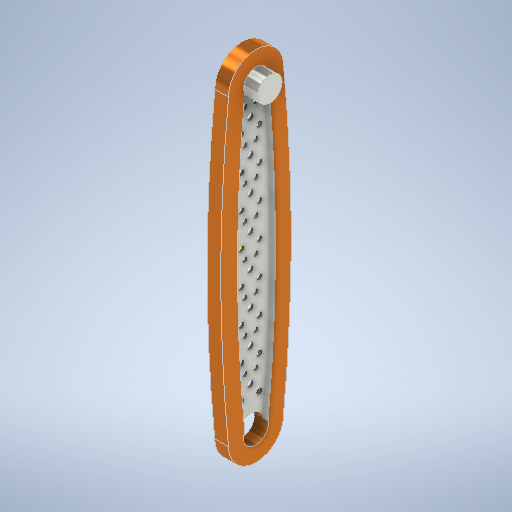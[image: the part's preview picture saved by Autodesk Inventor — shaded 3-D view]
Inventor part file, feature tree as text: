
AUTODESK INVENTOR PART (.ipt)
format: ipt  version: 2025 (Build 290162000, 162)  size: 450,560 bytes
history: native  units: in
note: dims shown in document units (in); Inventor stores cm internally (conversion verified against a paired STEP export)
features: sketch x6, extrude x5, pattern_linear x1
ambient origin geometry x8: Origin, YZ Plane, XZ Plane, XY Plane, X Axis, Y Axis, Z Axis, Center Point
bodies: Solid1 (feature_tree)
feature tree (12):
  extrude  "Extrusion1"  Depth=0.3543in
  sketch  "Sketch2"  dims[d5=0.3543in d6=4.3307in]
  extrude  "Extrusion2"  Depth=4.3307in
  extrude  "Extrusion3"  Depth=21.5399in
  extrude  "Extrusion4"  Depth=21.5399in
  pattern_linear  "Rectangular Pattern1"  Spacing1=0.1969in  [1 undecoded]
  extrude  "Extrusion5"  Depth=21.5411in
  sketch  "Sketch1"  dims[d2=0.7874in d4=0.3543in]
  sketch  "Sketch3"  dims[d7=21.5399in d8=4.3307in]
  sketch  "Sketch4"  dims[d9=21.5399in d10=0.7874in]
  sketch  "Sketch5"  dims[d11=1.0056in]
  sketch  "Sketch6"  dims[d12=0.1969in d13=0.0in d14=0.1969in d15=0.0in d16=21.5411in d17=21.5411in d18=21.5411in d19=21.5411in d20=0.0787in d21=0.0in d26=0.0394in d27=0.0394in d28=21.5411in d29=21.5411in d30=0.1575in d31=0.0787in d32=0.0787in d33=0.0984in d35=0.1181in d36=0.0in d37=0.0in d38=3.1496in d40=0.4724in d41=0.0866in d42=0.0866in d44=0.315in d45=0.2559in d46=0.1575in d47=0.2392in d48=0.2252in d50=0.3543in d51=21.5411in d52=0.1772in d53=21.5411in d54=0.0787in d55=0.0in]
note: 1 required parameter value undecoded (feature->parameter linkage not recoverable at this tier; creation-order binding heuristic only, values carry confidence <= 0.55)
